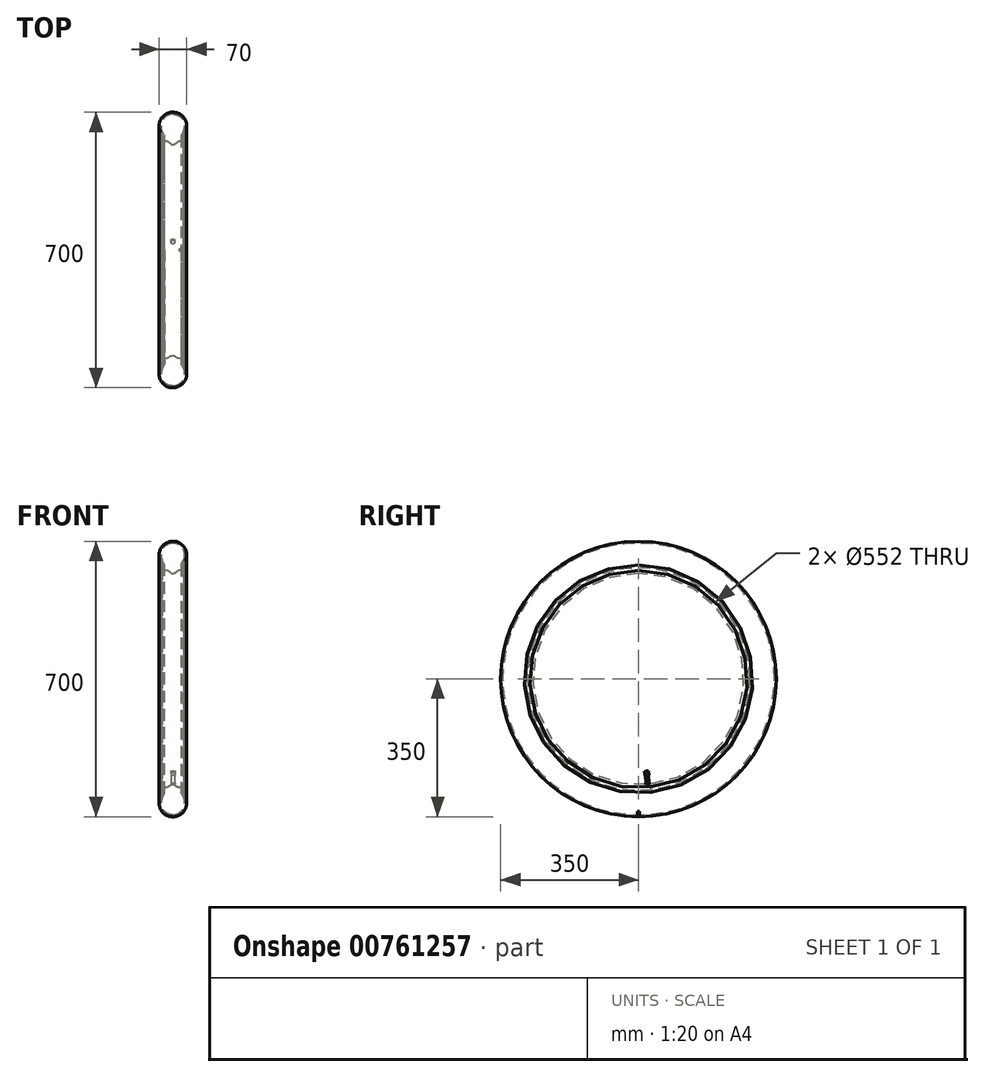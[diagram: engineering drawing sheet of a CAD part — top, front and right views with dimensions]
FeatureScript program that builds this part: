
annotation { "Feature Type Name" : "Feature", "Feature Type Description" : "" }
export const myFeature = defineFeature(function(context is Context, id is Id, definition is map)
    precondition{}
    {
        {
            var Q0;
            Q0=qCreatedBy(makeId("Front.planeOp"),FACE);
            var sketch = newSketch(context, id + "F0", { "sketchPlane" : qUnion([Q0])});
            skArc(sketch, "E0", {"start": v(5.8, -269.86) * mm, "mid": v(3.05, -268.48) * mm, "end": v(0, -268) * mm});
            skLineSegment(sketch, "E1", {"start": v(5.8, -269.86) * mm, "end": v(11.8, -274.14) * mm});
            skArc(sketch, "E2", {"start": v(11.8, -274.14) * mm, "mid": v(14.57, -275.52) * mm, "end": v(17.62, -276) * mm});
            skLineSegment(sketch, "E3", {"start": v(17.62, -276) * mm, "end": v(22.62, -276) * mm});
            skArc(sketch, "E4", {"start": v(27.38, -279.48) * mm, "mid": v(25.57, -276.96) * mm, "end": v(22.62, -276) * mm});
            skLineSegment(sketch, "E5", {"start": v(27.38, -279.48) * mm, "end": v(29.9, -287.4) * mm});
            skArc(sketch, "E6", {"start": v(29.9, -287.4) * mm, "mid": v(27.08, -289.78) * mm, "end": v(27.4, -286.1) * mm});
            skLineSegment(sketch, "E7", {"start": v(0, -315.08) * mm, "end": v(0, 0) * mm, "construction": true});
            skLineSegment(sketch, "E8", {"start": v(30, -286) * mm, "end": v(30, -290) * mm, "construction": true});
            skLineSegment(sketch, "E9", {"start": v(30, -290) * mm, "end": v(26, -290) * mm, "construction": true});
            skArc(sketch, "E10", {"start": v(27.4, -286.1) * mm, "mid": v(27.98, -285.6) * mm, "end": v(28.04, -284.84) * mm});
            skLineSegment(sketch, "E11", {"start": v(28, -288) * mm, "end": v(27.4, -286.1) * mm, "construction": true});
            skLineSegment(sketch, "E12", {"start": v(28.04, -284.84) * mm, "end": v(27.13, -281.98) * mm});
            skArc(sketch, "E13.MirrorCS", {"start": v(-5.8, -269.86) * mm, "mid": v(-3.05, -268.48) * mm, "end": v(0, -268) * mm});
            skLineSegment(sketch, "E14.MirrorCS", {"start": v(-5.8, -269.86) * mm, "end": v(-11.8, -274.14) * mm});
            skArc(sketch, "E15.MirrorCS", {"start": v(-11.8, -274.14) * mm, "mid": v(-14.57, -275.52) * mm, "end": v(-17.62, -276) * mm});
            skLineSegment(sketch, "E16.MirrorCS", {"start": v(-17.62, -276) * mm, "end": v(-22.62, -276) * mm});
            skArc(sketch, "E17.MirrorCS", {"start": v(-27.38, -279.48) * mm, "mid": v(-25.57, -276.96) * mm, "end": v(-22.62, -276) * mm});
            skLineSegment(sketch, "E18.MirrorCS", {"start": v(-27.38, -279.48) * mm, "end": v(-29.9, -287.4) * mm});
            skArc(sketch, "E19.MirrorCS", {"start": v(-29.9, -287.4) * mm, "mid": v(-27.08, -289.78) * mm, "end": v(-27.4, -286.1) * mm});
            skArc(sketch, "E20.MirrorCS", {"start": v(-27.4, -286.1) * mm, "mid": v(-27.98, -285.6) * mm, "end": v(-28.04, -284.84) * mm});
            skLineSegment(sketch, "E21.MirrorCS", {"start": v(-28.04, -284.84) * mm, "end": v(-27.13, -281.98) * mm});
            skArc(sketch, "E22.0", {"start": v(5.71, -270) * mm, "mid": v(3, -268.63) * mm, "end": v(0, -268.16) * mm});
            skLineSegment(sketch, "E22.1", {"start": v(5.71, -270) * mm, "end": v(11.71, -274.27) * mm});
            skArc(sketch, "E22.2", {"start": v(11.71, -274.27) * mm, "mid": v(14.52, -275.68) * mm, "end": v(17.62, -276.16) * mm});
            skLineSegment(sketch, "E22.3", {"start": v(17.62, -276.16) * mm, "end": v(22.62, -276.16) * mm});
            skArc(sketch, "E22.4", {"start": v(27.22, -279.53) * mm, "mid": v(25.47, -277.1) * mm, "end": v(22.62, -276.16) * mm});
            skLineSegment(sketch, "E22.5", {"start": v(28.2, -284.79) * mm, "end": v(27.28, -281.93) * mm});
            skArc(sketch, "E22.6", {"start": v(27.44, -286.25) * mm, "mid": v(28.12, -285.68) * mm, "end": v(28.2, -284.79) * mm});
            skArc(sketch, "E22.7", {"start": v(29.75, -287.44) * mm, "mid": v(27.16, -289.63) * mm, "end": v(27.44, -286.25) * mm});
            skLineSegment(sketch, "E22.8", {"start": v(27.22, -279.53) * mm, "end": v(29.75, -287.44) * mm});
            skLineSegment(sketch, "E23", {"start": v(27.28, -281.93) * mm, "end": v(27.13, -281.98) * mm});
            skArc(sketch, "E24.MirrorCS", {"start": v(-5.71, -270) * mm, "mid": v(-3, -268.63) * mm, "end": v(0, -268.16) * mm});
            skLineSegment(sketch, "E25.MirrorCS", {"start": v(-5.71, -270) * mm, "end": v(-11.71, -274.27) * mm});
            skArc(sketch, "E26.MirrorCS", {"start": v(-11.71, -274.27) * mm, "mid": v(-14.52, -275.68) * mm, "end": v(-17.62, -276.16) * mm});
            skLineSegment(sketch, "E27.MirrorCS", {"start": v(-17.62, -276.16) * mm, "end": v(-22.62, -276.16) * mm});
            skArc(sketch, "E28.MirrorCS", {"start": v(-27.22, -279.53) * mm, "mid": v(-25.47, -277.1) * mm, "end": v(-22.62, -276.16) * mm});
            skLineSegment(sketch, "E29.MirrorCS", {"start": v(-27.22, -279.53) * mm, "end": v(-29.75, -287.44) * mm});
            skArc(sketch, "E30.MirrorCS", {"start": v(-29.75, -287.44) * mm, "mid": v(-27.16, -289.63) * mm, "end": v(-27.44, -286.25) * mm});
            skArc(sketch, "E31.MirrorCS", {"start": v(-27.44, -286.25) * mm, "mid": v(-28.12, -285.68) * mm, "end": v(-28.2, -284.79) * mm});
            skLineSegment(sketch, "E32.MirrorCS", {"start": v(-28.2, -284.79) * mm, "end": v(-27.28, -281.93) * mm});
            skLineSegment(sketch, "E33.MirrorCS", {"start": v(-27.28, -281.93) * mm, "end": v(-27.13, -281.98) * mm});
            skPoint(sketch, "E34", {"position": v(28, -290) * mm});
            skPoint(sketch, "E35", {"position": v(30, -288) * mm});
            skLineSegment(sketch, "E36", {"start": v(-54, 0) * mm, "end": v(54, 0) * mm, "construction": true});
            skSolve(sketch);
        }
        {
            var Q0;
            Q0=qSketchRegion(id+"F0",true);
            var Q1;
            Q1=qConstructionFilter(qBodyType(qCreatedBy(id+"F0",EDGE),BodyType.WIRE),ConstructionObject.NO);
            var Q2;
            Q2=sQuery(id+"F0.wireOp",EDGE,"E36");
            revolve(context, id + "F1", {"surfaceOperationType" : NewSurfaceOperationType.NEW, "entities" : qUnion([Q0]), "surfaceEntities" : qUnion([Q1]), "axis" : qUnion([Q2]), "revolveType" : RevolveType.FULL});
        }
        {
            var Q0;
            Q0=qCreatedBy(makeId("Front.planeOp"),FACE);
            var sketch = newSketch(context, id + "F2", { "sketchPlane" : qUnion([Q0]), "disableImprinting" : false});
            skArc(sketch, "E37", {"start": v(0, -350) * mm, "mid": v(29.68, -333.55) * mm, "end": v(31.46, -299.66) * mm});
            skLineSegment(sketch, "E38", {"start": v(35, -315) * mm, "end": v(35, -262.1) * mm, "construction": true});
            skArc(sketch, "E39.MirrorCS", {"start": v(0, -350) * mm, "mid": v(-29.68, -333.55) * mm, "end": v(-31.46, -299.66) * mm});
            skLineSegment(sketch, "E40", {"start": v(31.46, -299.66) * mm, "end": v(26.2, -288.88) * mm});
            skLineSegment(sketch, "E41.MirrorCS", {"start": v(-31.46, -299.66) * mm, "end": v(-26.2, -288.88) * mm});
            skLineSegment(sketch, "E42.0", {"start": v(26.97, -301.85) * mm, "end": v(21.7, -291.07) * mm});
            skArc(sketch, "E42.1", {"start": v(0, -345) * mm, "mid": v(25.44, -330.9) * mm, "end": v(26.97, -301.85) * mm});
            skArc(sketch, "E43", {"start": v(26.2, -288.88) * mm, "mid": v(22.86, -287.72) * mm, "end": v(21.7, -291.07) * mm});
            skArc(sketch, "E44.MirrorCS", {"start": v(0, -345) * mm, "mid": v(-25.44, -330.9) * mm, "end": v(-26.97, -301.85) * mm});
            skLineSegment(sketch, "E45.MirrorCS", {"start": v(-26.97, -301.85) * mm, "end": v(-21.7, -291.07) * mm});
            skArc(sketch, "E46.MirrorCS", {"start": v(-26.2, -288.88) * mm, "mid": v(-22.86, -287.72) * mm, "end": v(-21.7, -291.07) * mm});
            skLineSegment(sketch, "E47", {"start": v(-4.64, -349.7) * mm, "end": v(-4.05, -346.84) * mm});
            skLineSegment(sketch, "E48", {"start": v(-4.05, -346.84) * mm, "end": v(-8.95, -345.83) * mm});
            skLineSegment(sketch, "E49", {"start": v(-8.95, -345.83) * mm, "end": v(-9.54, -348.67) * mm});
            skPoint(sketch, "E50", {"position": v(-6.5, -346.33) * mm});
            skLineSegment(sketch, "E51", {"start": v(0, -320.75) * mm, "end": v(0, -373.28) * mm, "construction": true});
            skLineSegment(sketch, "E52", {"start": v(-6.5, -346.33) * mm, "end": v(-7.1, -349.27) * mm, "construction": true});
            skLineSegment(sketch, "E53", {"start": v(-14.16, -347) * mm, "end": v(-12.8, -344.44) * mm});
            skLineSegment(sketch, "E54", {"start": v(-12.8, -344.44) * mm, "end": v(-17.2, -342.1) * mm});
            skLineSegment(sketch, "E55", {"start": v(-17.2, -342.1) * mm, "end": v(-18.57, -344.67) * mm});
            skPoint(sketch, "E56", {"position": v(-15, -343.27) * mm});
            skLineSegment(sketch, "E57", {"start": v(-15, -343.27) * mm, "end": v(-16.4, -345.92) * mm, "construction": true});
            skLineSegment(sketch, "E58.MirrorCS", {"start": v(17.2, -342.1) * mm, "end": v(18.57, -344.67) * mm});
            skLineSegment(sketch, "E59.MirrorCS", {"start": v(12.8, -344.44) * mm, "end": v(17.2, -342.1) * mm});
            skLineSegment(sketch, "E60.MirrorCS", {"start": v(14.16, -347) * mm, "end": v(12.8, -344.44) * mm});
            skLineSegment(sketch, "E61.MirrorCS", {"start": v(8.95, -345.83) * mm, "end": v(9.54, -348.67) * mm});
            skLineSegment(sketch, "E62.MirrorCS", {"start": v(4.05, -346.84) * mm, "end": v(8.95, -345.83) * mm});
            skLineSegment(sketch, "E63.MirrorCS", {"start": v(4.64, -349.7) * mm, "end": v(4.05, -346.84) * mm});
            skSolve(sketch);
        }
        {
            var Q0;
            {var subQ4=sQuery(id+"F2.wireOp",EDGE,"E40");Q0=makeQuery(id+"F2.imprint","IMPRINT",FACE,{"disambiguationData":[TD([[makeQuery(id+"F2.imprint","IMPRINT",EDGE,{"derivedFrom":subQ4}),1.0]])]});}
            var Q1;
            Q1=sQuery(id+"F2.wireOp",EDGE,"E37");
            var Q2;
            Q2=sQuery(id+"F2.wireOp",EDGE,"E40");
            var Q3;
            Q3=sQuery(id+"F2.wireOp",EDGE,"E39.MirrorCS");
            var Q4;
            Q4=sQuery(id+"F2.wireOp",EDGE,"E41.MirrorCS");
            var Q5;
            Q5=sQuery(id+"F0.wireOp",EDGE,"E36");
            revolve(context, id + "F3", {"surfaceOperationType" : NewSurfaceOperationType.NEW, "entities" : qUnion([Q0]), "surfaceEntities" : qUnion([Q1, Q2, Q3, Q4]), "axis" : qUnion([Q5]), "revolveType" : RevolveType.FULL});
        }
        {
            var Q0;
            Q0=qCreatedBy(makeId("Front.planeOp"),FACE);
            var sketch = newSketch(context, id + "F4", { "sketchPlane" : qUnion([Q0])});
            skLineSegment(sketch, "E64", {"start": v(0, -327.23) * mm, "end": v(0, -217.07) * mm, "construction": true});
            skLineSegment(sketch, "E65", {"start": v(-5, -268) * mm, "end": v(-5, -265) * mm});
            skLineSegment(sketch, "E66", {"start": v(-5, -265) * mm, "end": v(-4, -265) * mm});
            skLineSegment(sketch, "E67", {"start": v(-4, -265) * mm, "end": v(-4, -245) * mm});
            skLineSegment(sketch, "E68", {"start": v(-4, -245) * mm, "end": v(-5, -245) * mm});
            skLineSegment(sketch, "E69", {"start": v(-5, -245) * mm, "end": v(-5, -235) * mm});
            skArc(sketch, "E70", {"start": v(-5, -235) * mm, "mid": v(-3.54, -231.46) * mm, "end": v(0, -230) * mm});
            skLineSegment(sketch, "E71", {"start": v(-5, -268) * mm, "end": v(-4, -268) * mm});
            skLineSegment(sketch, "E72", {"start": v(0, -269.01) * mm, "end": v(0, -230) * mm});
            skLineSegment(sketch, "E73", {"start": v(-4, -268) * mm, "end": v(-4, -269.01) * mm});
            skLineSegment(sketch, "E74", {"start": v(-4, -269.01) * mm, "end": v(0, -269.01) * mm});
            skSolve(sketch);
        }
        {
            var Q0;
            Q0 = qSketchRegion(id + "F4", true);
            var Q1;
            Q1=sQuery(id+"F4.wireOp",EDGE,"E64");
            revolve(context, id + "F5", {"surfaceOperationType" : NewSurfaceOperationType.NEW, "entities" : qUnion([Q0]), "axis" : qUnion([Q1]), "revolveType" : RevolveType.FULL});
        }
        {
            var Q0;
            Q0=makeQuery(id+"F5.opRevolve","SWEPT_BODY",BODY,{"disambiguationData":[OSD([sQuery(id+"F4.wireOp",EDGE,"E65"),sQuery(id+"F4.wireOp",EDGE,"E66"),sQuery(id+"F4.wireOp",EDGE,"E67"),sQuery(id+"F4.wireOp",EDGE,"E68"),sQuery(id+"F4.wireOp",EDGE,"E69"),sQuery(id+"F4.wireOp",EDGE,"E70"),sQuery(id+"F4.wireOp",EDGE,"E71"),sQuery(id+"F4.wireOp",EDGE,"E72"),sQuery(id+"F4.wireOp",EDGE,"E73"),sQuery(id+"F4.wireOp",EDGE,"E74")])]});
            var Q1;
            Q1=sQuery(id+"F0.wireOp",EDGE,"E36");
            transform(context, id + "F6", {"entities" : qUnion([Q0]), "transformType" : TransformType.ROTATION, "transformAxis" : qUnion([Q1]), "angle" : 5 * degree, "makeCopy" : false});
        }
        {
            var Q0;
            Q0=qCreatedBy(makeId("Front.planeOp"),FACE);
            var sketch = newSketch(context, id + "F7", { "sketchPlane" : qUnion([Q0])});
            skLineSegment(sketch, "E75", {"start": v(0, -327.76) * mm, "end": v(0, -359.07) * mm, "construction": true});
            skLineSegment(sketch, "E76.0", {"start": v(17.2, -342.1) * mm, "end": v(18.57, -344.67) * mm});
            skLineSegment(sketch, "E77", {"start": v(17.2, -342.1) * mm, "end": v(30.84, -334.86) * mm});
            skLineSegment(sketch, "E78", {"start": v(30.84, -334.86) * mm, "end": v(33.88, -340.58) * mm});
            skLineSegment(sketch, "E79", {"start": v(18.57, -344.67) * mm, "end": v(20.25, -347.82) * mm});
            skLineSegment(sketch, "E80", {"start": v(20.25, -347.82) * mm, "end": v(33.88, -340.58) * mm});
            skSolve(sketch);
        }
        {
            var Q0;
            Q0 = qSketchRegion(id + "F7", true);
            extrude(context, id + "F8", {"entities" : qUnion([Q0]), "operationType" : NewBodyOperationType.REMOVE, "depth" : 6 * mm, "offsetDistance" : 25 * mm, "symmetric" : true});
        }
    });
